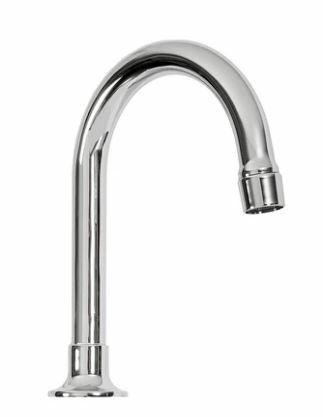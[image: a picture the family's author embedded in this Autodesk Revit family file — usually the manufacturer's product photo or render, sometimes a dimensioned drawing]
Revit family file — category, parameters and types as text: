
# Revit family: II-BR06-11-BRAZO ARCO MÓVIL LAVAMANOS
name_source: partatom
category: Plumbing Fixtures
revit_build: Autodesk Revit 2018 (Build: 20170223_1515(x64)
units: mm (PartAtom-declared; Revit-internal decimal feet)

## family parameters
Cut with Voids When Loaded = No
Host = Face
OmniClass Number = 23.31.11.00
Part Type = Normal
Room Calculation Point = No
Round Connector Dimension = Use Diameter
Shared = No

## types (1)
- II-BR06-11
    Alto = 168 mm
    Ancho = 54 mm  [stored 0.177165 ft]
    CW Connection = Yes
    Default Elevation = 0 mm  [stored 0 ft]
    Description = Brazo Griferia Lavamanos
    HW Connection = Yes
    Link Ficha Tecnica = https://infotecnica.gricol.com
    Manufacturer = Gricol
    Model = II-BR06-11
    Plastico ABS Cromado = Metal Laton Cromado
    Product Name = BRAZO ARCO MÓVIL LAVAMANOS
    Profundidad = 144.7 mm  [stored 0.474738 ft]
    Type Image = FOTO BRAZO ARCO MÓVIL LAVAMANOS.JPG
    URL = https://www.gricol.com
    Vent Connection = No
    Waste Connection = No

note: [stored X ft] marks values corroborated as IEEE doubles in the binary element streams (Revit-internal decimal feet)

## geometry (parser evidence)
native form markers: Blend x2, Sweep x5
no freeform markers — native parametric forms only
